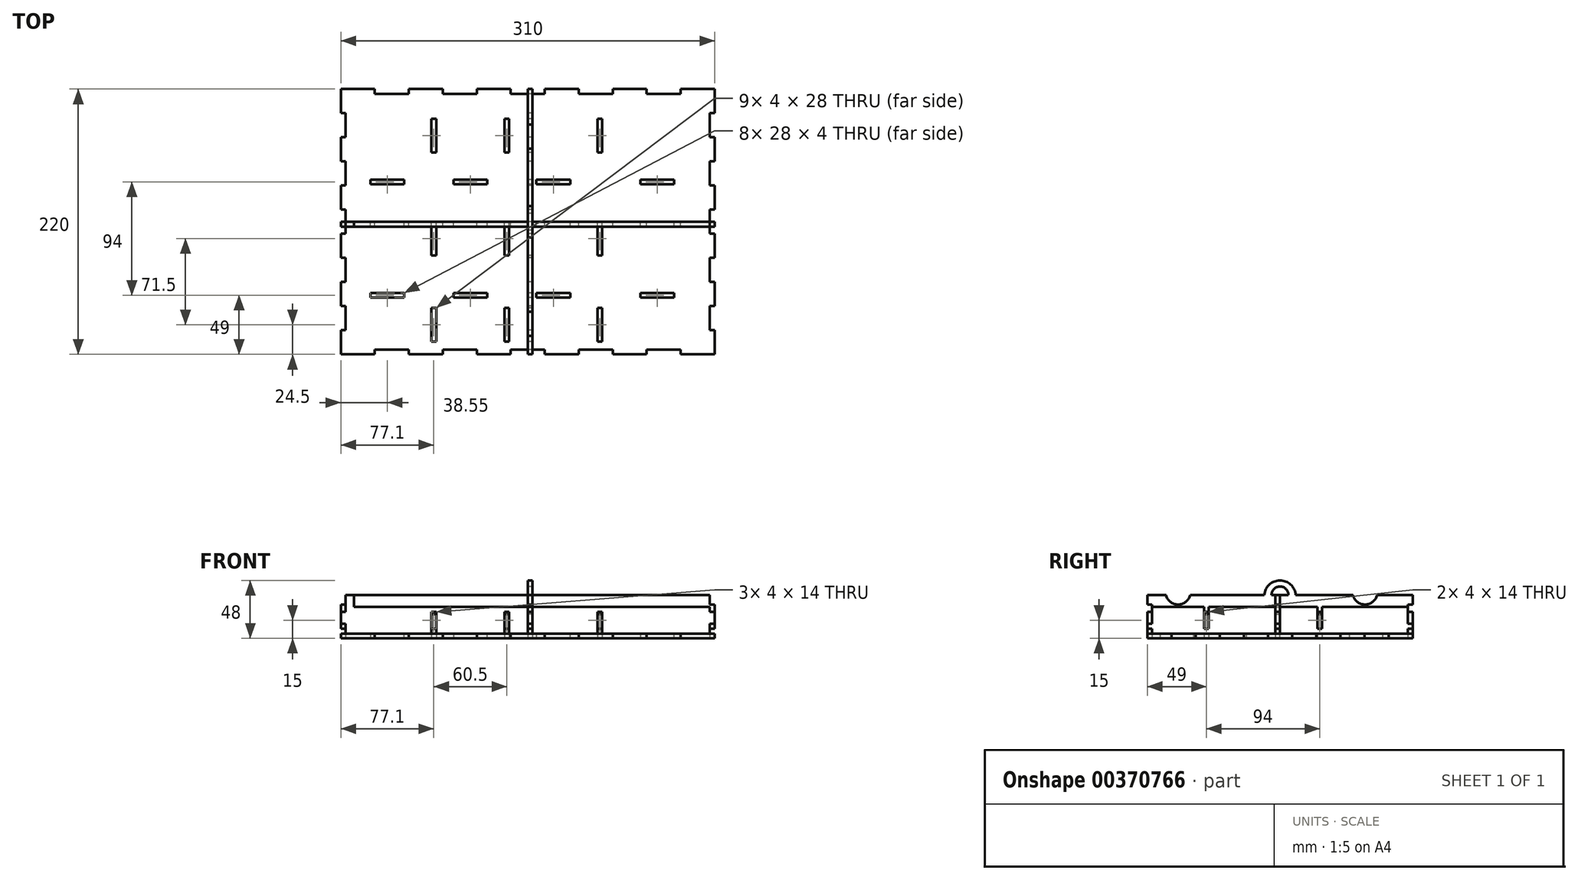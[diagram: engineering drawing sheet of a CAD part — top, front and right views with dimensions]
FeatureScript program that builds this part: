
annotation { "Feature Type Name" : "Feature", "Feature Type Description" : "" }
export const myFeature = defineFeature(function(context is Context, id is Id, definition is map)
    precondition{}
    {
        {
            var Q0;
            Q0=qCreatedBy(makeId("Top.planeOp"),FACE);
            var sketch = newSketch(context, id + "F0", { "sketchPlane" : qUnion([Q0])});
            skLineSegment(sketch, "E0", {"start": v(-155, 110) * mm, "end": v(-126.8, 110) * mm});
            skLineSegment(sketch, "E1", {"start": v(-126.8, 110) * mm, "end": v(-126.8, 106) * mm});
            skLineSegment(sketch, "E2", {"start": v(-126.8, 106) * mm, "end": v(-98.64, 106) * mm});
            skLineSegment(sketch, "E3", {"start": v(-155, 110) * mm, "end": v(-155, 90) * mm});
            skLineSegment(sketch, "E4", {"start": v(-155, 90) * mm, "end": v(-151, 90) * mm});
            skLineSegment(sketch, "E5", {"start": v(-151, 90) * mm, "end": v(-151, 70) * mm});
            skLineSegment(sketch, "E6", {"start": v(-151, 70) * mm, "end": v(-155, 70) * mm});
            skLineSegment(sketch, "E7", {"start": v(-98.64, 106) * mm, "end": v(-98.64, 110) * mm});
            skLineSegment(sketch, "E8.1.0.0", {"start": v(-98.64, 110) * mm, "end": v(-70.44, 110) * mm});
            skLineSegment(sketch, "E8.1.0.1", {"start": v(-70.44, 106) * mm, "end": v(-42.28, 106) * mm});
            skLineSegment(sketch, "E8.1.0.2", {"start": v(-42.28, 106) * mm, "end": v(-42.28, 110) * mm});
            skLineSegment(sketch, "E8.1.0.3", {"start": v(-70.44, 110) * mm, "end": v(-70.44, 106) * mm});
            skLineSegment(sketch, "E8.2.0.0", {"start": v(-42.28, 110) * mm, "end": v(-14.08, 110) * mm});
            skLineSegment(sketch, "E8.2.0.1", {"start": v(-14.08, 106) * mm, "end": v(14.08, 106) * mm});
            skLineSegment(sketch, "E8.2.0.2", {"start": v(14.08, 106) * mm, "end": v(14.08, 110) * mm});
            skLineSegment(sketch, "E8.2.0.3", {"start": v(-14.08, 110) * mm, "end": v(-14.08, 106) * mm});
            skLineSegment(sketch, "E8.3.0.0", {"start": v(14.08, 110) * mm, "end": v(42.28, 110) * mm});
            skLineSegment(sketch, "E8.3.0.1", {"start": v(42.28, 106) * mm, "end": v(70.44, 106) * mm});
            skLineSegment(sketch, "E8.3.0.2", {"start": v(70.44, 106) * mm, "end": v(70.44, 110) * mm});
            skLineSegment(sketch, "E8.3.0.3", {"start": v(42.28, 110) * mm, "end": v(42.28, 106) * mm});
            skLineSegment(sketch, "E8.4.0.0", {"start": v(70.44, 110) * mm, "end": v(98.64, 110) * mm});
            skLineSegment(sketch, "E8.4.0.1", {"start": v(98.64, 106) * mm, "end": v(126.8, 106) * mm});
            skLineSegment(sketch, "E8.4.0.2", {"start": v(126.8, 106) * mm, "end": v(126.8, 110) * mm});
            skLineSegment(sketch, "E8.4.0.3", {"start": v(98.64, 110) * mm, "end": v(98.64, 106) * mm});
            skLineSegment(sketch, "E8.5.0.0", {"start": v(126.8, 110) * mm, "end": v(155, 110) * mm});
            skLineSegment(sketch, "E8.direction1", {"start": v(-155, 110) * mm, "end": v(-98.64, 110) * mm, "construction": true});
            skLineSegment(sketch, "E9.0.1.0", {"start": v(-155, 70) * mm, "end": v(-155, 50) * mm});
            skLineSegment(sketch, "E9.0.1.1", {"start": v(-151, 50) * mm, "end": v(-151, 30) * mm});
            skLineSegment(sketch, "E9.0.1.2", {"start": v(-155, 50) * mm, "end": v(-151, 50) * mm});
            skLineSegment(sketch, "E9.0.1.3", {"start": v(-151, 30) * mm, "end": v(-155, 30) * mm});
            skLineSegment(sketch, "E9.0.2.0", {"start": v(-155, 30) * mm, "end": v(-155, 10) * mm});
            skLineSegment(sketch, "E9.0.2.1", {"start": v(-151, 10) * mm, "end": v(-151, -10) * mm});
            skLineSegment(sketch, "E9.0.2.2", {"start": v(-155, 10) * mm, "end": v(-151, 10) * mm});
            skLineSegment(sketch, "E9.0.2.3", {"start": v(-151, -10) * mm, "end": v(-155, -10) * mm});
            skLineSegment(sketch, "E9.0.3.0", {"start": v(-155, -10) * mm, "end": v(-155, -30) * mm});
            skLineSegment(sketch, "E9.0.3.1", {"start": v(-151, -30) * mm, "end": v(-151, -50) * mm});
            skLineSegment(sketch, "E9.0.3.2", {"start": v(-155, -30) * mm, "end": v(-151, -30) * mm});
            skLineSegment(sketch, "E9.0.3.3", {"start": v(-151, -50) * mm, "end": v(-155, -50) * mm});
            skLineSegment(sketch, "E9.0.4.0", {"start": v(-155, -50) * mm, "end": v(-155, -70) * mm});
            skLineSegment(sketch, "E9.0.4.1", {"start": v(-151, -70) * mm, "end": v(-151, -90) * mm});
            skLineSegment(sketch, "E9.0.4.2", {"start": v(-155, -70) * mm, "end": v(-151, -70) * mm});
            skLineSegment(sketch, "E9.0.4.3", {"start": v(-151, -90) * mm, "end": v(-155, -90) * mm});
            skLineSegment(sketch, "E9.0.5.0", {"start": v(-155, -90) * mm, "end": v(-155, -110) * mm});
            skLineSegment(sketch, "E9.direction1", {"start": v(-155, 70) * mm, "end": v(-124, 70) * mm, "construction": true});
            skLineSegment(sketch, "E9.direction2", {"start": v(-155, 70) * mm, "end": v(-155, 30) * mm, "construction": true});
            skLineSegment(sketch, "E10", {"start": v(155, 110) * mm, "end": v(155, 90) * mm});
            skLineSegment(sketch, "E11", {"start": v(155, 90) * mm, "end": v(151, 90) * mm});
            skLineSegment(sketch, "E12", {"start": v(151, 90) * mm, "end": v(151, 70) * mm});
            skLineSegment(sketch, "E13", {"start": v(151, 70) * mm, "end": v(155, 70) * mm});
            skLineSegment(sketch, "E14", {"start": v(-155, -110) * mm, "end": v(-126.8, -110) * mm});
            skLineSegment(sketch, "E15", {"start": v(-126.8, -110) * mm, "end": v(-126.8, -106) * mm});
            skLineSegment(sketch, "E16", {"start": v(-126.8, -106) * mm, "end": v(-98.64, -106) * mm});
            skLineSegment(sketch, "E17", {"start": v(-98.64, -106) * mm, "end": v(-98.64, -110) * mm});
            skLineSegment(sketch, "E18.1.0.0", {"start": v(-70.44, -106) * mm, "end": v(-42.28, -106) * mm});
            skLineSegment(sketch, "E18.1.0.1", {"start": v(-98.64, -110) * mm, "end": v(-70.44, -110) * mm});
            skLineSegment(sketch, "E18.1.0.2", {"start": v(-70.44, -110) * mm, "end": v(-70.44, -106) * mm});
            skLineSegment(sketch, "E18.1.0.3", {"start": v(-42.28, -106) * mm, "end": v(-42.28, -110) * mm});
            skLineSegment(sketch, "E18.2.0.0", {"start": v(-14.08, -106) * mm, "end": v(14.08, -106) * mm});
            skLineSegment(sketch, "E18.2.0.1", {"start": v(-42.28, -110) * mm, "end": v(-14.08, -110) * mm});
            skLineSegment(sketch, "E18.2.0.2", {"start": v(-14.08, -110) * mm, "end": v(-14.08, -106) * mm});
            skLineSegment(sketch, "E18.2.0.3", {"start": v(14.08, -106) * mm, "end": v(14.08, -110) * mm});
            skLineSegment(sketch, "E18.3.0.0", {"start": v(42.28, -106) * mm, "end": v(70.44, -106) * mm});
            skLineSegment(sketch, "E18.3.0.1", {"start": v(14.08, -110) * mm, "end": v(42.28, -110) * mm});
            skLineSegment(sketch, "E18.3.0.2", {"start": v(42.28, -110) * mm, "end": v(42.28, -106) * mm});
            skLineSegment(sketch, "E18.3.0.3", {"start": v(70.44, -106) * mm, "end": v(70.44, -110) * mm});
            skLineSegment(sketch, "E18.4.0.0", {"start": v(98.64, -106) * mm, "end": v(126.8, -106) * mm});
            skLineSegment(sketch, "E18.4.0.1", {"start": v(70.44, -110) * mm, "end": v(98.64, -110) * mm});
            skLineSegment(sketch, "E18.4.0.2", {"start": v(98.64, -110) * mm, "end": v(98.64, -106) * mm});
            skLineSegment(sketch, "E18.4.0.3", {"start": v(126.8, -106) * mm, "end": v(126.8, -110) * mm});
            skLineSegment(sketch, "E18.5.0.1", {"start": v(126.8, -110) * mm, "end": v(155, -110) * mm});
            skLineSegment(sketch, "E18.direction1", {"start": v(-155, -110) * mm, "end": v(-98.64, -110) * mm, "construction": true});
            skLineSegment(sketch, "E19.0.1.0", {"start": v(151, 50) * mm, "end": v(151, 30) * mm});
            skLineSegment(sketch, "E19.0.1.1", {"start": v(155, 70) * mm, "end": v(155, 50) * mm});
            skLineSegment(sketch, "E19.0.1.2", {"start": v(155, 50) * mm, "end": v(151, 50) * mm});
            skLineSegment(sketch, "E19.0.1.3", {"start": v(151, 30) * mm, "end": v(155, 30) * mm});
            skLineSegment(sketch, "E19.0.2.0", {"start": v(151, 10) * mm, "end": v(151, -10) * mm});
            skLineSegment(sketch, "E19.0.2.1", {"start": v(155, 30) * mm, "end": v(155, 10) * mm});
            skLineSegment(sketch, "E19.0.2.2", {"start": v(155, 10) * mm, "end": v(151, 10) * mm});
            skLineSegment(sketch, "E19.0.2.3", {"start": v(151, -10) * mm, "end": v(155, -10) * mm});
            skLineSegment(sketch, "E19.0.3.0", {"start": v(151, -30) * mm, "end": v(151, -50) * mm});
            skLineSegment(sketch, "E19.0.3.1", {"start": v(155, -10) * mm, "end": v(155, -30) * mm});
            skLineSegment(sketch, "E19.0.3.2", {"start": v(155, -30) * mm, "end": v(151, -30) * mm});
            skLineSegment(sketch, "E19.0.3.3", {"start": v(151, -50) * mm, "end": v(155, -50) * mm});
            skLineSegment(sketch, "E19.0.4.0", {"start": v(151, -70) * mm, "end": v(151, -90) * mm});
            skLineSegment(sketch, "E19.0.4.1", {"start": v(155, -50) * mm, "end": v(155, -70) * mm});
            skLineSegment(sketch, "E19.0.4.2", {"start": v(155, -70) * mm, "end": v(151, -70) * mm});
            skLineSegment(sketch, "E19.0.4.3", {"start": v(151, -90) * mm, "end": v(155, -90) * mm});
            skLineSegment(sketch, "E19.0.5.1", {"start": v(155, -90) * mm, "end": v(155, -110) * mm});
            skLineSegment(sketch, "E19.direction1", {"start": v(151, 70) * mm, "end": v(171.43, 70) * mm, "construction": true});
            skLineSegment(sketch, "E19.direction2", {"start": v(151, 70) * mm, "end": v(151, 30) * mm, "construction": true});
            skLineSegment(sketch, "E20", {"start": v(176.81, -61) * mm, "end": v(-206.45, -61) * mm, "construction": true});
            skLineSegment(sketch, "E21", {"start": v(220.81, 33) * mm, "end": v(-162.45, 33) * mm, "construction": true});
            skLineSegment(sketch, "E22", {"start": v(59.8, 157.7) * mm, "end": v(59.8, -215.6) * mm, "construction": true});
            skLineSegment(sketch, "E23", {"start": v(-17.4, 160.3) * mm, "end": v(-17.4, -213) * mm, "construction": true});
            skLineSegment(sketch, "E24", {"start": v(-77.9, 160.3) * mm, "end": v(-77.9, -213) * mm, "construction": true});
            skLineSegment(sketch, "E25.bottom", {"start": v(-15.4, 85.5) * mm, "end": v(-19.4, 85.5) * mm});
            skLineSegment(sketch, "E25.top", {"start": v(-15.4, 57.5) * mm, "end": v(-19.4, 57.5) * mm});
            skLineSegment(sketch, "E25.left", {"start": v(-15.4, 85.5) * mm, "end": v(-15.4, 57.5) * mm});
            skLineSegment(sketch, "E25.right", {"start": v(-19.4, 85.5) * mm, "end": v(-19.4, 57.5) * mm});
            skLineSegment(sketch, "E26.bottom", {"start": v(-15.4, 0) * mm, "end": v(-19.4, 0) * mm});
            skLineSegment(sketch, "E26.top", {"start": v(-15.4, -28) * mm, "end": v(-19.4, -28) * mm});
            skLineSegment(sketch, "E26.left", {"start": v(-15.4, 0) * mm, "end": v(-15.4, -28) * mm});
            skLineSegment(sketch, "E26.right", {"start": v(-19.4, 0) * mm, "end": v(-19.4, -28) * mm});
            skLineSegment(sketch, "E27.bottom", {"start": v(-15.4, -71.5) * mm, "end": v(-19.4, -71.5) * mm});
            skLineSegment(sketch, "E27.top", {"start": v(-15.4, -99.5) * mm, "end": v(-19.4, -99.5) * mm});
            skLineSegment(sketch, "E27.left", {"start": v(-15.4, -71.5) * mm, "end": v(-15.4, -99.5) * mm});
            skLineSegment(sketch, "E27.right", {"start": v(-19.4, -71.5) * mm, "end": v(-19.4, -99.5) * mm});
            skLineSegment(sketch, "E28.1.0.0", {"start": v(-75.9, 0) * mm, "end": v(-75.9, -28) * mm});
            skLineSegment(sketch, "E28.1.0.1", {"start": v(-79.9, 0) * mm, "end": v(-79.9, -28) * mm});
            skLineSegment(sketch, "E28.1.0.2", {"start": v(-75.9, -71.5) * mm, "end": v(-75.9, -99.5) * mm});
            skLineSegment(sketch, "E28.1.0.3", {"start": v(-75.9, 85.5) * mm, "end": v(-75.9, 57.5) * mm});
            skLineSegment(sketch, "E28.1.0.4", {"start": v(-79.9, -71.5) * mm, "end": v(-79.9, -99.5) * mm});
            skLineSegment(sketch, "E28.1.0.5", {"start": v(-79.9, 85.5) * mm, "end": v(-79.9, 57.5) * mm});
            skLineSegment(sketch, "E28.1.0.6", {"start": v(-75.9, -99.5) * mm, "end": v(-79.9, -99.5) * mm});
            skLineSegment(sketch, "E28.1.0.7", {"start": v(-75.9, -71.5) * mm, "end": v(-79.9, -71.5) * mm});
            skLineSegment(sketch, "E28.1.0.8", {"start": v(-75.9, 0) * mm, "end": v(-79.9, 0) * mm});
            skLineSegment(sketch, "E28.1.0.10", {"start": v(-75.9, -28) * mm, "end": v(-79.9, -28) * mm});
            skLineSegment(sketch, "E28.1.0.11", {"start": v(-75.9, 85.5) * mm, "end": v(-79.9, 85.5) * mm});
            skLineSegment(sketch, "E28.1.0.12", {"start": v(-75.9, 57.5) * mm, "end": v(-79.9, 57.5) * mm});
            skLineSegment(sketch, "E28.direction1", {"start": v(-19.4, -99.5) * mm, "end": v(-79.9, -99.5) * mm, "construction": true});
            skLineSegment(sketch, "E29.1.0.0", {"start": v(57.8, 0) * mm, "end": v(57.8, -28) * mm});
            skLineSegment(sketch, "E29.1.0.1", {"start": v(57.8, -71.5) * mm, "end": v(57.8, -99.5) * mm});
            skLineSegment(sketch, "E29.1.0.2", {"start": v(61.8, -71.5) * mm, "end": v(61.8, -99.5) * mm});
            skLineSegment(sketch, "E29.1.0.3", {"start": v(61.8, 0) * mm, "end": v(61.8, -28) * mm});
            skLineSegment(sketch, "E29.1.0.4", {"start": v(57.8, 85.5) * mm, "end": v(57.8, 57.5) * mm});
            skLineSegment(sketch, "E29.1.0.5", {"start": v(61.8, 85.5) * mm, "end": v(61.8, 57.5) * mm});
            skLineSegment(sketch, "E29.1.0.6", {"start": v(61.8, 85.5) * mm, "end": v(57.8, 85.5) * mm});
            skLineSegment(sketch, "E29.1.0.7", {"start": v(61.8, 57.5) * mm, "end": v(57.8, 57.5) * mm});
            skLineSegment(sketch, "E29.1.0.8", {"start": v(61.8, -71.5) * mm, "end": v(57.8, -71.5) * mm});
            skLineSegment(sketch, "E29.1.0.11", {"start": v(61.8, -28) * mm, "end": v(57.8, -28) * mm});
            skLineSegment(sketch, "E29.1.0.12", {"start": v(61.8, 0) * mm, "end": v(57.8, 0) * mm});
            skLineSegment(sketch, "E29.1.0.13", {"start": v(61.8, -99.5) * mm, "end": v(57.8, -99.5) * mm});
            skLineSegment(sketch, "E29.direction1", {"start": v(-19.4, -99.5) * mm, "end": v(57.8, -99.5) * mm, "construction": true});
            skLineSegment(sketch, "E30.bottom", {"start": v(121.4, 35) * mm, "end": v(93.4, 35) * mm});
            skLineSegment(sketch, "E30.top", {"start": v(121.4, 31) * mm, "end": v(93.4, 31) * mm});
            skLineSegment(sketch, "E30.left", {"start": v(121.4, 35) * mm, "end": v(121.4, 31) * mm});
            skLineSegment(sketch, "E30.right", {"start": v(93.4, 35) * mm, "end": v(93.4, 31) * mm});
            skLineSegment(sketch, "E31.bottom", {"start": v(35.2, 31) * mm, "end": v(7.2, 31) * mm});
            skLineSegment(sketch, "E31.top", {"start": v(35.2, 35) * mm, "end": v(7.2, 35) * mm});
            skLineSegment(sketch, "E31.left", {"start": v(35.2, 31) * mm, "end": v(35.2, 35) * mm});
            skLineSegment(sketch, "E31.right", {"start": v(7.2, 31) * mm, "end": v(7.2, 35) * mm});
            skLineSegment(sketch, "E32.bottom", {"start": v(-33.65, 35) * mm, "end": v(-61.65, 35) * mm});
            skLineSegment(sketch, "E32.top", {"start": v(-33.65, 31) * mm, "end": v(-61.65, 31) * mm});
            skLineSegment(sketch, "E32.left", {"start": v(-33.65, 35) * mm, "end": v(-33.65, 31) * mm});
            skLineSegment(sketch, "E32.right", {"start": v(-61.65, 35) * mm, "end": v(-61.65, 31) * mm});
            skLineSegment(sketch, "E33.bottom", {"start": v(-102.45, 31) * mm, "end": v(-130.45, 31) * mm});
            skLineSegment(sketch, "E33.top", {"start": v(-102.45, 35) * mm, "end": v(-130.45, 35) * mm});
            skLineSegment(sketch, "E33.left", {"start": v(-102.45, 31) * mm, "end": v(-102.45, 35) * mm});
            skLineSegment(sketch, "E33.right", {"start": v(-130.45, 31) * mm, "end": v(-130.45, 35) * mm});
            skLineSegment(sketch, "E34.0.1.0", {"start": v(-33.65, -59) * mm, "end": v(-61.65, -59) * mm});
            skLineSegment(sketch, "E34.0.1.1", {"start": v(-102.45, -59) * mm, "end": v(-130.45, -59) * mm});
            skLineSegment(sketch, "E34.0.1.2", {"start": v(35.2, -63) * mm, "end": v(7.2, -63) * mm});
            skLineSegment(sketch, "E34.0.1.3", {"start": v(121.4, -63) * mm, "end": v(93.4, -63) * mm});
            skLineSegment(sketch, "E34.0.1.4", {"start": v(35.2, -59) * mm, "end": v(7.2, -59) * mm});
            skLineSegment(sketch, "E34.0.1.5", {"start": v(121.4, -59) * mm, "end": v(93.4, -59) * mm});
            skLineSegment(sketch, "E34.0.1.6", {"start": v(-33.65, -63) * mm, "end": v(-61.65, -63) * mm});
            skLineSegment(sketch, "E34.0.1.7", {"start": v(-102.45, -63) * mm, "end": v(-130.45, -63) * mm});
            skLineSegment(sketch, "E34.0.1.8", {"start": v(35.2, -63) * mm, "end": v(35.2, -59) * mm});
            skLineSegment(sketch, "E34.0.1.9", {"start": v(121.4, -59) * mm, "end": v(121.4, -63) * mm});
            skLineSegment(sketch, "E34.0.1.10", {"start": v(93.4, -59) * mm, "end": v(93.4, -63) * mm});
            skLineSegment(sketch, "E34.0.1.11", {"start": v(-102.45, -63) * mm, "end": v(-102.45, -59) * mm});
            skLineSegment(sketch, "E34.0.1.12", {"start": v(-130.45, -63) * mm, "end": v(-130.45, -59) * mm});
            skLineSegment(sketch, "E34.0.1.13", {"start": v(7.2, -63) * mm, "end": v(7.2, -59) * mm});
            skLineSegment(sketch, "E34.0.1.14", {"start": v(-33.65, -59) * mm, "end": v(-33.65, -63) * mm});
            skLineSegment(sketch, "E34.0.1.15", {"start": v(-61.65, -59) * mm, "end": v(-61.65, -63) * mm});
            skLineSegment(sketch, "E34.direction1", {"start": v(-130.45, 31) * mm, "end": v(-110.22, 31) * mm, "construction": true});
            skLineSegment(sketch, "E34.direction2", {"start": v(-130.45, 31) * mm, "end": v(-130.45, -63) * mm, "construction": true});
            skSolve(sketch);
        }
        {
            var Q0;
            Q0 = qSketchRegion(id + "F0", true);
            extrude(context, id + "F1", {"entities" : qUnion([Q0]), "depth" : 4 * mm});
        }
        {
            var Q0;
            Q0=qCreatedBy(makeId("Front.planeOp"),FACE);
            var sketch = newSketch(context, id + "F2", { "sketchPlane" : qUnion([Q0])});
            skLineSegment(sketch, "E35", {"start": v(-151, 26) * mm, "end": v(-151, 22) * mm});
            skLineSegment(sketch, "E36", {"start": v(-151, 22) * mm, "end": v(-155, 22) * mm});
            skLineSegment(sketch, "E37", {"start": v(-155, 22) * mm, "end": v(-155, 8) * mm});
            skLineSegment(sketch, "E38", {"start": v(-155, 8) * mm, "end": v(-151, 8) * mm});
            skLineSegment(sketch, "E39", {"start": v(-151, 8) * mm, "end": v(-151, 4) * mm});
            skLineSegment(sketch, "E40", {"start": v(151, 4) * mm, "end": v(151, 8) * mm});
            skLineSegment(sketch, "E41", {"start": v(151, 8) * mm, "end": v(155, 8) * mm});
            skLineSegment(sketch, "E42", {"start": v(155, 8) * mm, "end": v(155, 22) * mm});
            skLineSegment(sketch, "E43", {"start": v(155, 22) * mm, "end": v(151, 22) * mm});
            skLineSegment(sketch, "E44", {"start": v(151, 22) * mm, "end": v(151, 26) * mm});
            skLineSegment(sketch, "E45", {"start": v(151, 26) * mm, "end": v(-151, 26) * mm});
            skLineSegment(sketch, "E46", {"start": v(-151, 4) * mm, "end": v(-130.45, 4) * mm});
            skLineSegment(sketch, "E47", {"start": v(-130.45, 4) * mm, "end": v(-130.45, 0) * mm});
            skLineSegment(sketch, "E48", {"start": v(-130.45, 0) * mm, "end": v(-102.45, 0) * mm});
            skLineSegment(sketch, "E49", {"start": v(-102.45, 0) * mm, "end": v(-102.45, 4) * mm});
            skLineSegment(sketch, "E50", {"start": v(-61.65, 4) * mm, "end": v(-61.65, 0) * mm});
            skLineSegment(sketch, "E51", {"start": v(-61.65, 0) * mm, "end": v(-33.65, 0) * mm});
            skLineSegment(sketch, "E52", {"start": v(-33.65, 0) * mm, "end": v(-33.65, 4) * mm});
            skLineSegment(sketch, "E53", {"start": v(7.2, 4) * mm, "end": v(7.2, 0) * mm});
            skLineSegment(sketch, "E54", {"start": v(7.2, 0) * mm, "end": v(35.2, 0) * mm});
            skLineSegment(sketch, "E55", {"start": v(35.2, 0) * mm, "end": v(35.2, 4) * mm});
            skLineSegment(sketch, "E56", {"start": v(93.4, 4) * mm, "end": v(93.4, 0) * mm});
            skLineSegment(sketch, "E57", {"start": v(93.4, 0) * mm, "end": v(121.4, 0) * mm});
            skLineSegment(sketch, "E58", {"start": v(121.4, 0) * mm, "end": v(121.4, 4) * mm});
            skLineSegment(sketch, "E59", {"start": v(121.4, 4) * mm, "end": v(151, 4) * mm});
            skLineSegment(sketch, "E60", {"start": v(-79.9, 4) * mm, "end": v(-79.9, 20) * mm});
            skLineSegment(sketch, "E61", {"start": v(-79.9, 20) * mm, "end": v(-75.9, 20) * mm});
            skLineSegment(sketch, "E62", {"start": v(-75.9, 20) * mm, "end": v(-75.9, 4) * mm});
            skLineSegment(sketch, "E63", {"start": v(-75.9, 4) * mm, "end": v(-61.65, 4) * mm});
            skLineSegment(sketch, "E64", {"start": v(-79.9, 4) * mm, "end": v(-102.45, 4) * mm});
            skLineSegment(sketch, "E65", {"start": v(-33.65, 4) * mm, "end": v(-19.4, 4) * mm});
            skLineSegment(sketch, "E66", {"start": v(-19.4, 4) * mm, "end": v(-19.4, 20) * mm});
            skLineSegment(sketch, "E67", {"start": v(-19.4, 20) * mm, "end": v(-15.4, 20) * mm});
            skLineSegment(sketch, "E68", {"start": v(-15.4, 20) * mm, "end": v(-15.4, 4) * mm});
            skLineSegment(sketch, "E69", {"start": v(-15.4, 4) * mm, "end": v(7.2, 4) * mm});
            skLineSegment(sketch, "E70", {"start": v(35.2, 4) * mm, "end": v(57.8, 4) * mm});
            skLineSegment(sketch, "E71", {"start": v(57.8, 4) * mm, "end": v(57.8, 20) * mm});
            skLineSegment(sketch, "E72", {"start": v(57.8, 20) * mm, "end": v(61.8, 20) * mm});
            skLineSegment(sketch, "E73", {"start": v(61.8, 20) * mm, "end": v(61.8, 4) * mm});
            skLineSegment(sketch, "E74", {"start": v(61.8, 4) * mm, "end": v(93.4, 4) * mm});
            skLineSegment(sketch, "E75.bottom", {"start": v(-151, 26) * mm, "end": v(-144, 26) * mm});
            skLineSegment(sketch, "E75.top", {"start": v(-151, 36) * mm, "end": v(-144, 36) * mm});
            skLineSegment(sketch, "E75.left", {"start": v(-151, 26) * mm, "end": v(-151, 36) * mm});
            skLineSegment(sketch, "E75.right", {"start": v(-144, 26) * mm, "end": v(-144, 36) * mm});
            skSolve(sketch);
        }
        {
            var Q0;
            Q0 = qSketchRegion(id + "F2", true);
            extrude(context, id + "F3", {"entities" : qUnion([Q0]), "depth" : 4 * mm});
        }
        {
            var Q0;
            Q0=qCreatedBy(makeId("Right.planeOp"),FACE);
            var sketch = newSketch(context, id + "F4", { "sketchPlane" : qUnion([Q0])});
            skLineSegment(sketch, "E76", {"start": v(-99.5, 4) * mm, "end": v(-99.5, 0) * mm});
            skLineSegment(sketch, "E77", {"start": v(-99.5, 0) * mm, "end": v(-71.5, 0) * mm});
            skLineSegment(sketch, "E78", {"start": v(-71.5, 0) * mm, "end": v(-71.5, 4) * mm});
            skLineSegment(sketch, "E79", {"start": v(-71.5, 4) * mm, "end": v(-28, 4) * mm});
            skLineSegment(sketch, "E80", {"start": v(-28, 4) * mm, "end": v(-28, 0) * mm});
            skLineSegment(sketch, "E81", {"start": v(-28, 0) * mm, "end": v(0, 0) * mm});
            skLineSegment(sketch, "E82", {"start": v(0, 0) * mm, "end": v(0, 4) * mm});
            skLineSegment(sketch, "E83", {"start": v(0, 4) * mm, "end": v(57.5, 4) * mm});
            skLineSegment(sketch, "E84", {"start": v(57.5, 4) * mm, "end": v(57.5, 0) * mm});
            skLineSegment(sketch, "E85", {"start": v(57.5, 0) * mm, "end": v(85.5, 0) * mm});
            skLineSegment(sketch, "E86", {"start": v(85.5, 0) * mm, "end": v(85.5, 4) * mm});
            skLineSegment(sketch, "E87", {"start": v(-99.5, 4) * mm, "end": v(-106, 4) * mm});
            skLineSegment(sketch, "E88", {"start": v(-106, 4) * mm, "end": v(-106, 8) * mm});
            skLineSegment(sketch, "E89", {"start": v(-106, 8) * mm, "end": v(-110, 8) * mm});
            skLineSegment(sketch, "E90", {"start": v(-110, 8) * mm, "end": v(-110, 22) * mm});
            skLineSegment(sketch, "E91", {"start": v(-110, 22) * mm, "end": v(-106, 22) * mm});
            skLineSegment(sketch, "E92", {"start": v(-106, 22) * mm, "end": v(-106, 26) * mm});
            skLineSegment(sketch, "E93", {"start": v(-106, 26) * mm, "end": v(-63, 26) * mm});
            skLineSegment(sketch, "E94", {"start": v(-59, 26) * mm, "end": v(31, 26) * mm});
            skLineSegment(sketch, "E95", {"start": v(106, 26) * mm, "end": v(106, 22) * mm});
            skLineSegment(sketch, "E96", {"start": v(106, 22) * mm, "end": v(110, 22) * mm});
            skLineSegment(sketch, "E97", {"start": v(110, 22) * mm, "end": v(110, 8) * mm});
            skLineSegment(sketch, "E98", {"start": v(110, 8) * mm, "end": v(106, 8) * mm});
            skLineSegment(sketch, "E99", {"start": v(106, 8) * mm, "end": v(106, 4) * mm});
            skLineSegment(sketch, "E100", {"start": v(106, 4) * mm, "end": v(85.5, 4) * mm});
            skLineSegment(sketch, "E101", {"start": v(-63, 26) * mm, "end": v(-63, 20) * mm});
            skLineSegment(sketch, "E102", {"start": v(-63, 20) * mm, "end": v(-59, 20) * mm});
            skLineSegment(sketch, "E103", {"start": v(-59, 20) * mm, "end": v(-59, 26) * mm});
            skLineSegment(sketch, "E104", {"start": v(31, 26) * mm, "end": v(31, 20) * mm});
            skLineSegment(sketch, "E105", {"start": v(31, 20) * mm, "end": v(35, 20) * mm});
            skLineSegment(sketch, "E106", {"start": v(35, 20) * mm, "end": v(35, 26) * mm});
            skLineSegment(sketch, "E107", {"start": v(35, 26) * mm, "end": v(106, 26) * mm});
            skSolve(sketch);
        }
        {
            var Q0;
            Q0 = qSketchRegion(id + "F4", true);
            extrude(context, id + "F5", {"entities" : qUnion([Q0]), "depth" : 4 * mm});
        }
        {
            var Q0;
            Q0=qCreatedBy(makeId("Front.planeOp"),FACE);
            var sketch = newSketch(context, id + "F6", { "sketchPlane" : qUnion([Q0])});
            skLineSegment(sketch, "E108", {"start": v(-151, 36) * mm, "end": v(-151, 28) * mm});
            skLineSegment(sketch, "E109", {"start": v(-151, 28) * mm, "end": v(-155, 28) * mm});
            skLineSegment(sketch, "E110", {"start": v(-155, 28) * mm, "end": v(-155, 12) * mm});
            skLineSegment(sketch, "E111", {"start": v(-155, 12) * mm, "end": v(-151, 12) * mm});
            skLineSegment(sketch, "E112", {"start": v(-151, 12) * mm, "end": v(-151, 4) * mm});
            skLineSegment(sketch, "E113", {"start": v(-151, 4) * mm, "end": v(-126.8, 4) * mm});
            skLineSegment(sketch, "E114", {"start": v(-126.8, 4) * mm, "end": v(-126.8, 0) * mm});
            skLineSegment(sketch, "E115", {"start": v(-126.8, 0) * mm, "end": v(-98.64, 0) * mm});
            skLineSegment(sketch, "E116", {"start": v(-98.64, 0) * mm, "end": v(-98.64, 4) * mm});
            skLineSegment(sketch, "E117", {"start": v(-98.64, 4) * mm, "end": v(-70.44, 4) * mm});
            skLineSegment(sketch, "E118", {"start": v(-70.44, 4) * mm, "end": v(-70.44, 0) * mm});
            skLineSegment(sketch, "E119", {"start": v(-70.44, 0) * mm, "end": v(-42.28, 0) * mm});
            skLineSegment(sketch, "E120", {"start": v(-42.28, 0) * mm, "end": v(-42.28, 4) * mm});
            skLineSegment(sketch, "E121", {"start": v(-42.28, 4) * mm, "end": v(-14.08, 4) * mm});
            skLineSegment(sketch, "E122", {"start": v(-14.08, 4) * mm, "end": v(-14.08, 0) * mm});
            skLineSegment(sketch, "E123", {"start": v(42.28, 0) * mm, "end": v(42.28, 4) * mm});
            skLineSegment(sketch, "E124", {"start": v(14.08, 4) * mm, "end": v(42.28, 4) * mm});
            skLineSegment(sketch, "E125", {"start": v(14.08, 4) * mm, "end": v(14.08, 0) * mm});
            skLineSegment(sketch, "E126", {"start": v(70.44, 0) * mm, "end": v(70.44, 4) * mm});
            skLineSegment(sketch, "E127", {"start": v(70.44, 4) * mm, "end": v(98.64, 4) * mm});
            skLineSegment(sketch, "E128", {"start": v(98.64, 4) * mm, "end": v(98.64, 0) * mm});
            skLineSegment(sketch, "E129", {"start": v(98.64, 0) * mm, "end": v(126.8, 0) * mm});
            skLineSegment(sketch, "E130", {"start": v(126.8, 0) * mm, "end": v(126.8, 4) * mm});
            skLineSegment(sketch, "E131", {"start": v(126.8, 4) * mm, "end": v(151, 4) * mm});
            skLineSegment(sketch, "E132", {"start": v(151, 4) * mm, "end": v(151, 12) * mm});
            skLineSegment(sketch, "E133", {"start": v(151, 12) * mm, "end": v(155, 12) * mm});
            skLineSegment(sketch, "E134", {"start": v(155, 12) * mm, "end": v(155, 28) * mm});
            skLineSegment(sketch, "E135", {"start": v(155, 28) * mm, "end": v(151, 28) * mm});
            skLineSegment(sketch, "E136", {"start": v(151, 28) * mm, "end": v(151, 36) * mm});
            skLineSegment(sketch, "E137", {"start": v(151, 36) * mm, "end": v(-151, 36) * mm});
            skLineSegment(sketch, "E138", {"start": v(-14.08, 0) * mm, "end": v(14.08, 0) * mm});
            skLineSegment(sketch, "E139", {"start": v(42.28, 0) * mm, "end": v(70.44, 0) * mm});
            skLineSegment(sketch, "E140.bottom", {"start": v(-79.9, 22) * mm, "end": v(-75.9, 22) * mm});
            skLineSegment(sketch, "E140.top", {"start": v(-79.9, 8) * mm, "end": v(-75.9, 8) * mm});
            skLineSegment(sketch, "E140.left", {"start": v(-79.9, 22) * mm, "end": v(-79.9, 8) * mm});
            skLineSegment(sketch, "E140.right", {"start": v(-75.9, 22) * mm, "end": v(-75.9, 8) * mm});
            skLineSegment(sketch, "E141.bottom", {"start": v(-19.4, 22) * mm, "end": v(-15.4, 22) * mm});
            skLineSegment(sketch, "E141.top", {"start": v(-19.4, 8) * mm, "end": v(-15.4, 8) * mm});
            skLineSegment(sketch, "E141.left", {"start": v(-19.4, 22) * mm, "end": v(-19.4, 8) * mm});
            skLineSegment(sketch, "E141.right", {"start": v(-15.4, 22) * mm, "end": v(-15.4, 8) * mm});
            skLineSegment(sketch, "E142.bottom", {"start": v(57.8, 8) * mm, "end": v(61.8, 8) * mm});
            skLineSegment(sketch, "E142.top", {"start": v(57.8, 22) * mm, "end": v(61.8, 22) * mm});
            skLineSegment(sketch, "E142.left", {"start": v(57.8, 8) * mm, "end": v(57.8, 22) * mm});
            skLineSegment(sketch, "E142.right", {"start": v(61.8, 8) * mm, "end": v(61.8, 22) * mm});
            skSolve(sketch);
        }
        {
            var Q0;
            Q0 = qSketchRegion(id + "F6", true);
            extrude(context, id + "F7", {"entities" : qUnion([Q0]), "depth" : 4 * mm});
        }
        {
            var Q0;
            Q0=qCreatedBy(makeId("Right.planeOp"),FACE);
            var sketch = newSketch(context, id + "F8", { "sketchPlane" : qUnion([Q0])});
            skLineSegment(sketch, "E143", {"start": v(-110, 12) * mm, "end": v(-106, 12) * mm});
            skLineSegment(sketch, "E144", {"start": v(-106, 12) * mm, "end": v(-106, 28) * mm});
            skLineSegment(sketch, "E145", {"start": v(-106, 28) * mm, "end": v(-110, 28) * mm});
            skLineSegment(sketch, "E146", {"start": v(-110, 28) * mm, "end": v(-110, 36) * mm});
            skLineSegment(sketch, "E147", {"start": v(-110, 36) * mm, "end": v(-94.5, 36) * mm});
            skLineSegment(sketch, "E148", {"start": v(-74.5, 36) * mm, "end": v(-13, 36) * mm});
            skLineSegment(sketch, "E149", {"start": v(13, 36) * mm, "end": v(60.5, 36) * mm});
            skLineSegment(sketch, "E150", {"start": v(80.5, 36) * mm, "end": v(110, 36) * mm});
            skLineSegment(sketch, "E151", {"start": v(110, 36) * mm, "end": v(110, 28) * mm});
            skLineSegment(sketch, "E152", {"start": v(110, 28) * mm, "end": v(106, 28) * mm});
            skLineSegment(sketch, "E153", {"start": v(106, 28) * mm, "end": v(106, 12) * mm});
            skLineSegment(sketch, "E154", {"start": v(106, 12) * mm, "end": v(110, 12) * mm});
            skLineSegment(sketch, "E155", {"start": v(-110, 12) * mm, "end": v(-110, 4) * mm});
            skLineSegment(sketch, "E156", {"start": v(-110, 4) * mm, "end": v(-90, 4) * mm});
            skLineSegment(sketch, "E157", {"start": v(-90, 4) * mm, "end": v(-90, 0) * mm});
            skLineSegment(sketch, "E158", {"start": v(-90, 0) * mm, "end": v(-70, 0) * mm});
            skLineSegment(sketch, "E159", {"start": v(-70, 0) * mm, "end": v(-70, 4) * mm});
            skLineSegment(sketch, "E160", {"start": v(-70, 4) * mm, "end": v(-50, 4) * mm});
            skLineSegment(sketch, "E161", {"start": v(-50, 4) * mm, "end": v(-50, 0) * mm});
            skLineSegment(sketch, "E162", {"start": v(-50, 0) * mm, "end": v(-30, 0) * mm});
            skLineSegment(sketch, "E163", {"start": v(-30, 0) * mm, "end": v(-30, 4) * mm});
            skLineSegment(sketch, "E164", {"start": v(-30, 4) * mm, "end": v(-10, 4) * mm});
            skLineSegment(sketch, "E165", {"start": v(-10, 4) * mm, "end": v(-10, 0) * mm});
            skLineSegment(sketch, "E166", {"start": v(-10, 0) * mm, "end": v(10, 0) * mm});
            skLineSegment(sketch, "E167", {"start": v(10, 0) * mm, "end": v(10, 4) * mm});
            skLineSegment(sketch, "E168", {"start": v(10, 4) * mm, "end": v(30, 4) * mm});
            skLineSegment(sketch, "E169", {"start": v(30, 4) * mm, "end": v(30, 0) * mm});
            skLineSegment(sketch, "E170", {"start": v(30, 0) * mm, "end": v(50, 0) * mm});
            skLineSegment(sketch, "E171", {"start": v(50, 0) * mm, "end": v(50, 4) * mm});
            skLineSegment(sketch, "E172", {"start": v(50, 4) * mm, "end": v(70, 4) * mm});
            skLineSegment(sketch, "E173", {"start": v(70, 4) * mm, "end": v(70, 0) * mm});
            skLineSegment(sketch, "E174", {"start": v(70, 0) * mm, "end": v(90, 0) * mm});
            skLineSegment(sketch, "E175", {"start": v(90, 0) * mm, "end": v(90, 4) * mm});
            skLineSegment(sketch, "E176", {"start": v(90, 4) * mm, "end": v(110, 4) * mm});
            skLineSegment(sketch, "E177", {"start": v(110, 4) * mm, "end": v(110, 12) * mm});
            skArc(sketch, "E178", {"start": v(13, 36) * mm, "mid": v(0, 48) * mm, "end": v(-13, 36) * mm});
            skLineSegment(sketch, "E179", {"start": v(-84.5, 48) * mm, "end": v(70.5, 48) * mm, "construction": true});
            skArc(sketch, "E180", {"start": v(-94.5, 36) * mm, "mid": v(-84.5, 28) * mm, "end": v(-74.5, 36) * mm});
            skArc(sketch, "E181", {"start": v(60.5, 36) * mm, "mid": v(70.5, 28) * mm, "end": v(80.5, 36) * mm});
            skLineSegment(sketch, "E182", {"start": v(-84.5, 28) * mm, "end": v(70.5, 28) * mm, "construction": true});
            skLineSegment(sketch, "E183", {"start": v(-84.5, 38.25) * mm, "end": v(-84.5, 28) * mm, "construction": true});
            skLineSegment(sketch, "E184", {"start": v(70.5, 38.25) * mm, "end": v(70.5, 28) * mm, "construction": true});
            skLineSegment(sketch, "E185.bottom", {"start": v(-63, 8) * mm, "end": v(-59, 8) * mm});
            skLineSegment(sketch, "E185.top", {"start": v(-63, 22) * mm, "end": v(-59, 22) * mm});
            skLineSegment(sketch, "E185.left", {"start": v(-63, 8) * mm, "end": v(-63, 22) * mm});
            skLineSegment(sketch, "E185.right", {"start": v(-59, 8) * mm, "end": v(-59, 22) * mm});
            skLineSegment(sketch, "E186.bottom", {"start": v(31, 8) * mm, "end": v(35, 8) * mm});
            skLineSegment(sketch, "E186.top", {"start": v(31, 22) * mm, "end": v(35, 22) * mm});
            skLineSegment(sketch, "E186.left", {"start": v(31, 8) * mm, "end": v(31, 22) * mm});
            skLineSegment(sketch, "E186.right", {"start": v(35, 8) * mm, "end": v(35, 22) * mm});
            skLineSegment(sketch, "E187", {"start": v(-7, 36) * mm, "end": v(7, 36) * mm});
            skArc(sketch, "E188", {"start": v(7, 36) * mm, "mid": v(0, 43) * mm, "end": v(-7, 36) * mm});
            skLineSegment(sketch, "E189", {"start": v(35, 22) * mm, "end": v(70.5, 22) * mm, "construction": true});
            skLineSegment(sketch, "E190", {"start": v(70.5, 22) * mm, "end": v(106, 22) * mm, "construction": true});
            skLineSegment(sketch, "E191", {"start": v(-63, 22) * mm, "end": v(-84.5, 22) * mm, "construction": true});
            skLineSegment(sketch, "E192", {"start": v(-84.5, 22) * mm, "end": v(-106, 22) * mm, "construction": true});
            skLineSegment(sketch, "E193", {"start": v(-13, 36) * mm, "end": v(-7, 36) * mm, "construction": true});
            skLineSegment(sketch, "E194", {"start": v(7, 36) * mm, "end": v(13, 36) * mm, "construction": true});
            skSolve(sketch);
        }
        {
            var Q0;
            Q0 = qSketchRegion(id + "F8", true);
            extrude(context, id + "F9", {"entities" : qUnion([Q0]), "depth" : 4 * mm});
        }
    });
